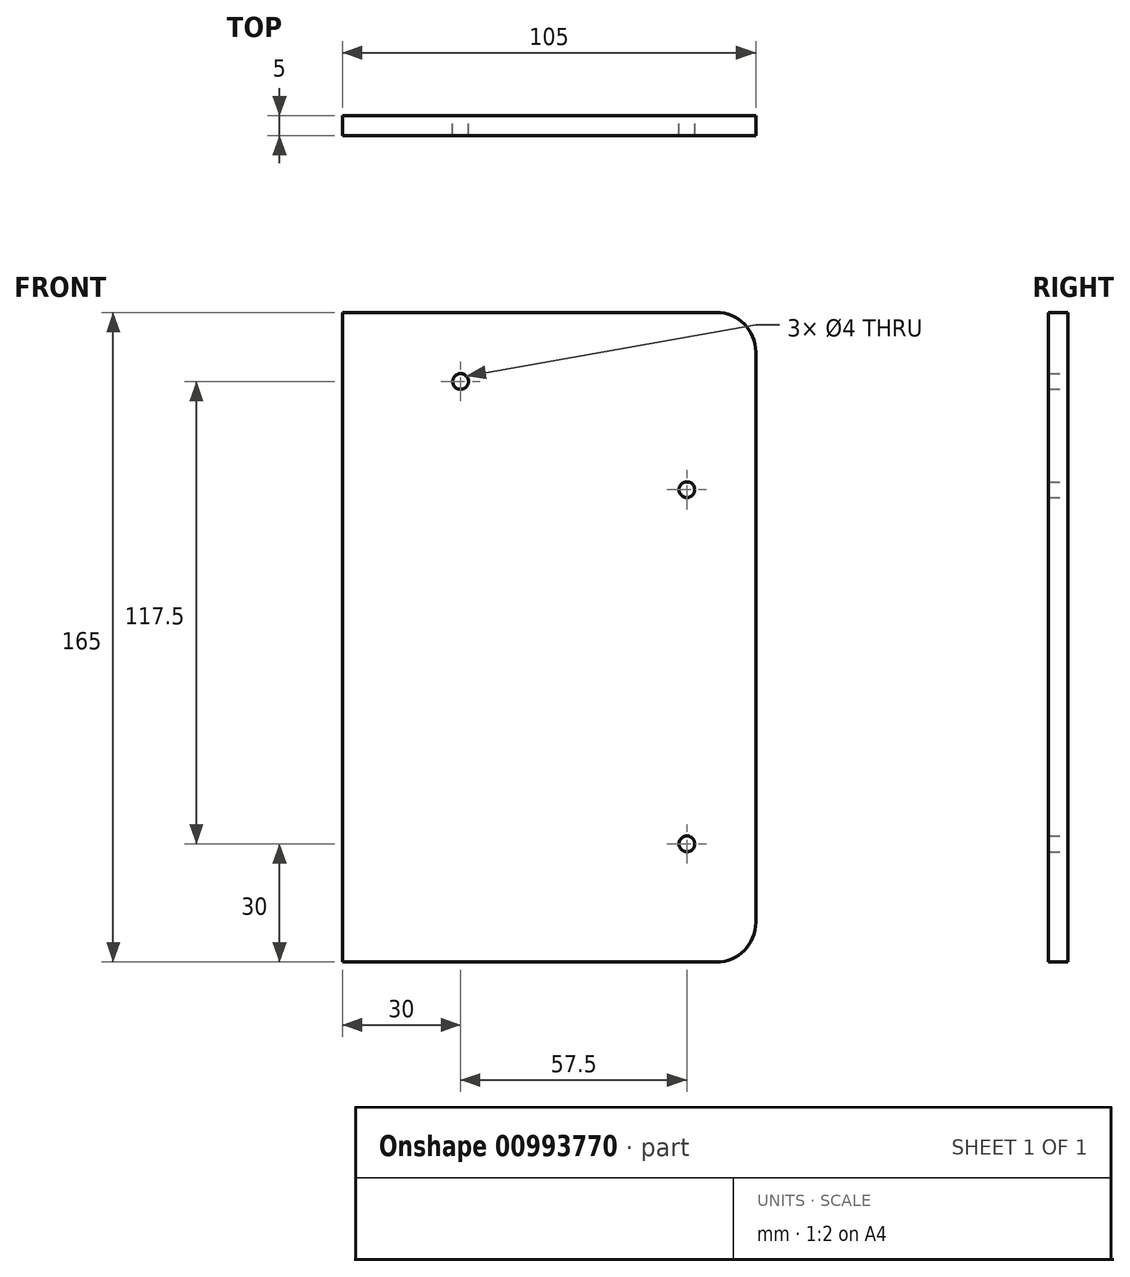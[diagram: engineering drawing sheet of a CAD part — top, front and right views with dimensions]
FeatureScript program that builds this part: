
annotation { "Feature Type Name" : "Feature", "Feature Type Description" : "" }
export const myFeature = defineFeature(function(context is Context, id is Id, definition is map)
    precondition{}
    {
        {
            var Q0;
            Q0=qCreatedBy(makeId("Front.planeOp"),FACE);
            var sketch = newSketch(context, id + "F0", { "sketchPlane" : qUnion([Q0])});
            skLineSegment(sketch, "E0.bottom", {"start": v(0, 0) * mm, "end": v(95, 0) * mm});
            skLineSegment(sketch, "E0.top", {"start": v(0, 165) * mm, "end": v(95, 165) * mm});
            skLineSegment(sketch, "E0.left", {"start": v(0, 0) * mm, "end": v(0, 165) * mm});
            skLineSegment(sketch, "E0.right", {"start": v(105, 10) * mm, "end": v(105, 155) * mm});
            skArc(sketch, "E1", {"start": v(105, 155) * mm, "mid": v(102.07, 162.07) * mm, "end": v(95, 165) * mm});
            skPoint(sketch, "E2.visualSharp", {"position": v(105, 0) * mm});
            skArc(sketch, "E2.filletArc", {"start": v(95, 0) * mm, "mid": v(102.07, 2.93) * mm, "end": v(105, 10) * mm});
            skCircle(sketch, "E3", {"center": v(30, 147.5) * mm, "radius": 2 * mm});
            skCircle(sketch, "E4", {"center": v(87.5, 120) * mm, "radius": 2 * mm});
            skCircle(sketch, "E5", {"center": v(87.5, 30) * mm, "radius": 2 * mm});
            skLineSegment(sketch, "E6", {"start": v(87.5, 120) * mm, "end": v(87.5, 30) * mm});
            skSolve(sketch);
        }
        {
            var Q0;
            Q0=makeQuery(id+"F0.imprint","IMPRINT",FACE,{"disambiguationData":[TD([[makeQuery(id+"F0.imprint","IMPRINT",EDGE,{"derivedFrom":sQuery(id+"F0.wireOp",EDGE,"E0.bottom")}),1.0]])]});
            extrude(context, id + "F1", {"entities" : qUnion([Q0]), "depth" : 5 * mm, "offsetDistance" : 25 * mm});
        }
    });
